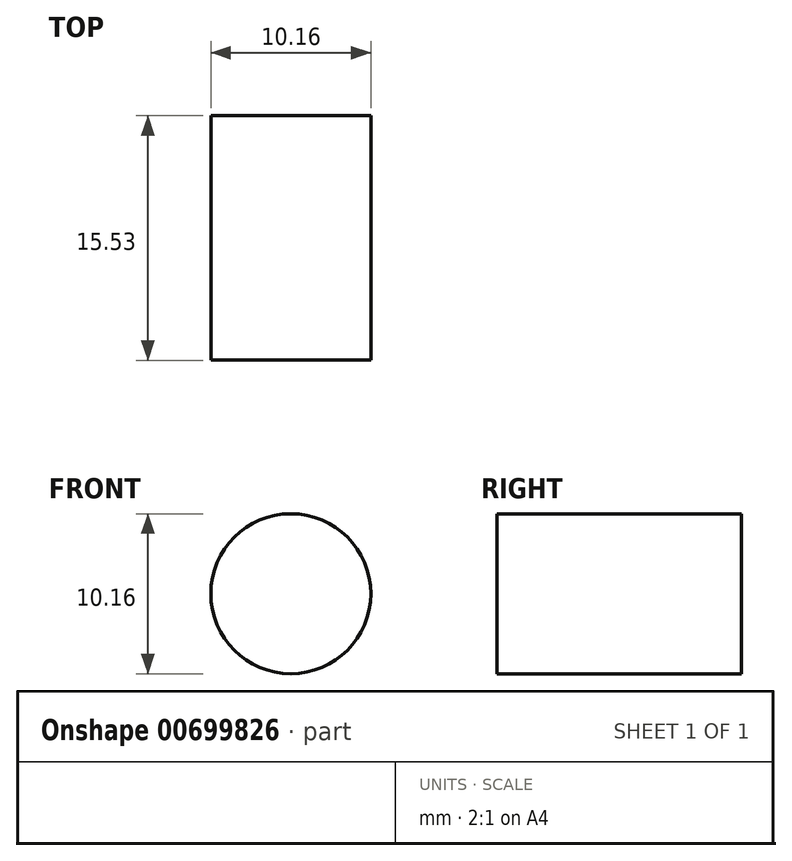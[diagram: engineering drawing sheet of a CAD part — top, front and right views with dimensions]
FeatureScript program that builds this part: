
annotation { "Feature Type Name" : "Feature", "Feature Type Description" : "" }
export const myFeature = defineFeature(function(context is Context, id is Id, definition is map)
    precondition{}
    {
        {
            var Q0;
            Q0=qCreatedBy(makeId("Front.planeOp"),FACE);
            var sketch = newSketch(context, id + "F0", { "sketchPlane" : qUnion([Q0])});
            skCircle(sketch, "E0", {"center": v(0, 0) * mm, "radius": 5.08 * mm});
            skSolve(sketch);
        }
        {
            var Q0;
            Q0=qSketchRegion(id+"F0",true);
            extrude(context, id + "F1", {"entities" : qUnion([Q0]), "depth" : 15.53 * mm});
        }
    });
